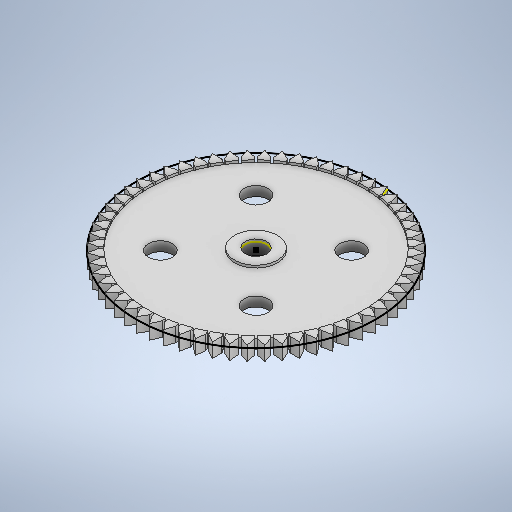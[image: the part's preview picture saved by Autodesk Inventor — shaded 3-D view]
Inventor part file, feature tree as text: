
AUTODESK INVENTOR PART (.ipt)
format: ipt  version: 2025.2 (Build 292293000, 293)  size: 629,760 bytes
history: native  units: mm
features: sketch x4, extrude x3, pattern_circular x1
ambient origin geometry x8: Origin, YZ Plane, XZ Plane, XY Plane, X Axis, Y Axis, Z Axis, Center Point
bodies: Solid1 (feature_tree)
feature tree (8):
  extrude  "Extrusion1"  Depth=45.0mm
  extrude  "Extrusion2"  Depth=4.5mm
  pattern_circular  "Circular Pattern1"  Count=2  [1 undecoded]
  extrude  "Extrusion3"  Depth=5.0mm
  sketch  "Sketch4"  dims[d7=5.0mm d8=5.0mm d9=2.0mm d10=0.0mm d11=50.0mm d12=2.0mm d13=30.0deg d14=2.0mm d15=0.5mm d16=2.5mm d17=0.0mm d18=0.0mm d19=600.0mm d20=360.0deg d22=9.0mm d23=0.5mm d24=2.5mm d25=0.0mm d26=0.0mm]
  sketch  "Sketch1"  dims[d0=50.0mm d1=45.0mm]
  sketch  "Sketch2"  dims[d2=4.5mm d3=20.0mm d4=20.0mm]
  sketch  "Sketch3"  dims[d5=5.0mm d6=5.0mm]
note: 1 required parameter value undecoded (feature->parameter linkage not recoverable at this tier; creation-order binding heuristic only, values carry confidence <= 0.55)
